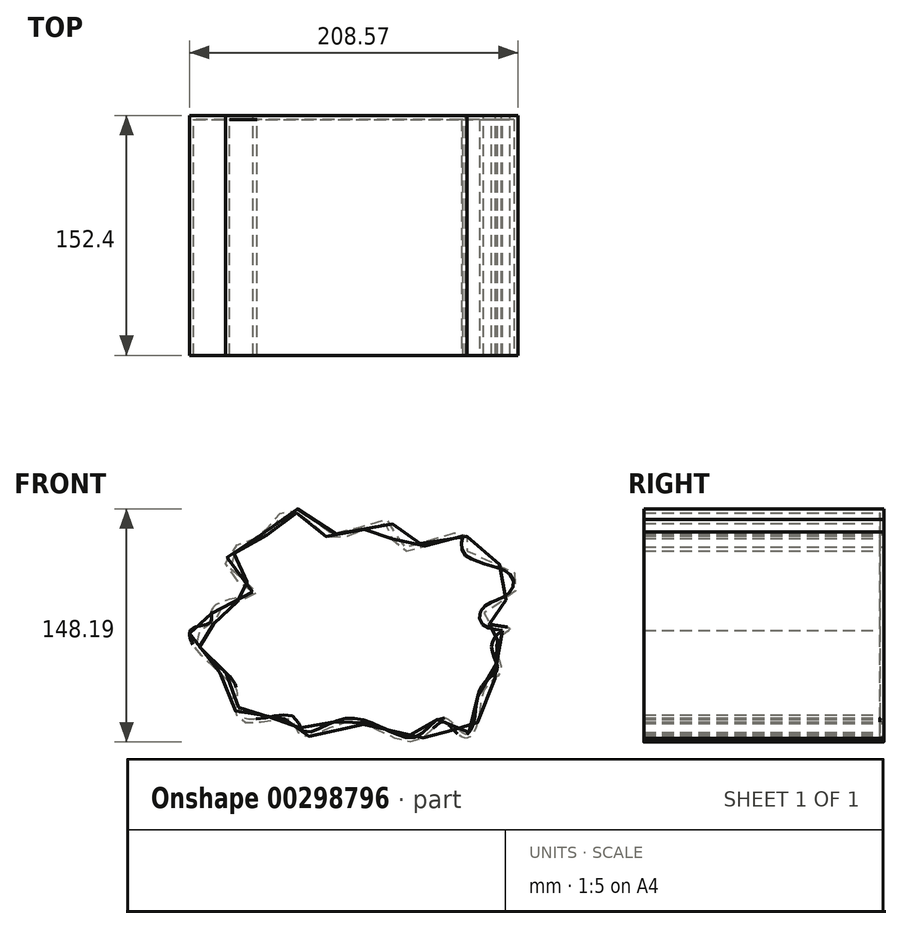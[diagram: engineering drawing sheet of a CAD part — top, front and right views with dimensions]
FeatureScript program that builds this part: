
annotation { "Feature Type Name" : "Feature", "Feature Type Description" : "" }
export const myFeature = defineFeature(function(context is Context, id is Id, definition is map)
    precondition{}
    {
        {
            var Q0;
            Q0=qCreatedBy(makeId("Front.planeOp"),FACE);
            var sketch = newSketch(context, id + "F0", { "sketchPlane" : qUnion([Q0])});
            skFitSpline(sketch, "E0", {"points": [v(-69.7, 23.3) * mm, v(-86.06, 36.1) * mm, v(-78.24, 53.88) * mm, v(-65.44, 58.5) * mm, v(-53.35, 72.37) * mm, v(-35.2, 73.8) * mm, v(-19.2, 59.92) * mm, v(16.71, 68.82) * mm, v(23.12, 53.52) * mm, v(41.6, 55.66) * mm, v(66.15, 60.28) * mm, v(65.8, 49.97) * mm, v(95.67, 36.1) * mm, v(94.95, 20.8) * mm, v(78.24, 11.2) * mm, v(78.95, 3.73) * mm, v(93.53, 0) * mm, v(85, -9.07) * mm, v(88.2, -26.14) * mm, v(78.24, -37.52) * mm, v(72.9, -60.64) * mm, v(65.8, -69.88) * mm, v(56.9, -63.48) * mm, v(49.79, -59.57) * mm, v(32.72, -72.02) * mm, v(-5.7, -59.57) * mm, v(-33.43, -68.46) * mm, v(-41.6, -64.9) * mm, v(-45.88, -57.8) * mm, v(-76.46, -59.21) * mm, v(-82.15, -40.36) * mm, v(-88.55, -30.05) * mm, v(-107.76, -10.14) * mm, v(-108.11, 0) * mm, v(-96.73, 4.09) * mm, v(-93.89, 14.4) * mm, v(-69.7, 23.3) * mm]});
            skSolve(sketch);
        }
        {
            var Q0;
            Q0=makeQuery(id+"F0.imprint","IMPRINT",FACE,{"disambiguationData":[TD([[makeQuery(id+"F0.imprint","IMPRINT",EDGE,{"derivedFrom":sQuery(id+"F0.wireOp",EDGE,"E0")}),-1.0]])]});
            extrude(context, id + "F1", {"entities" : qUnion([Q0]), "depth" : 152.4 * mm});
        }
        {
            var Q0;
            Q0=makeQuery(id+"F1.opExtrude","CAP_FACE",FACE,{"disambiguationData":[OSD([sQuery(id+"F0.wireOp",EDGE,"E0")])],"isStart":false});
            shell(context, id + "F2", {"entities" : qUnion([Q0]), "thickness" : 2.54 * mm});
        }
    });
